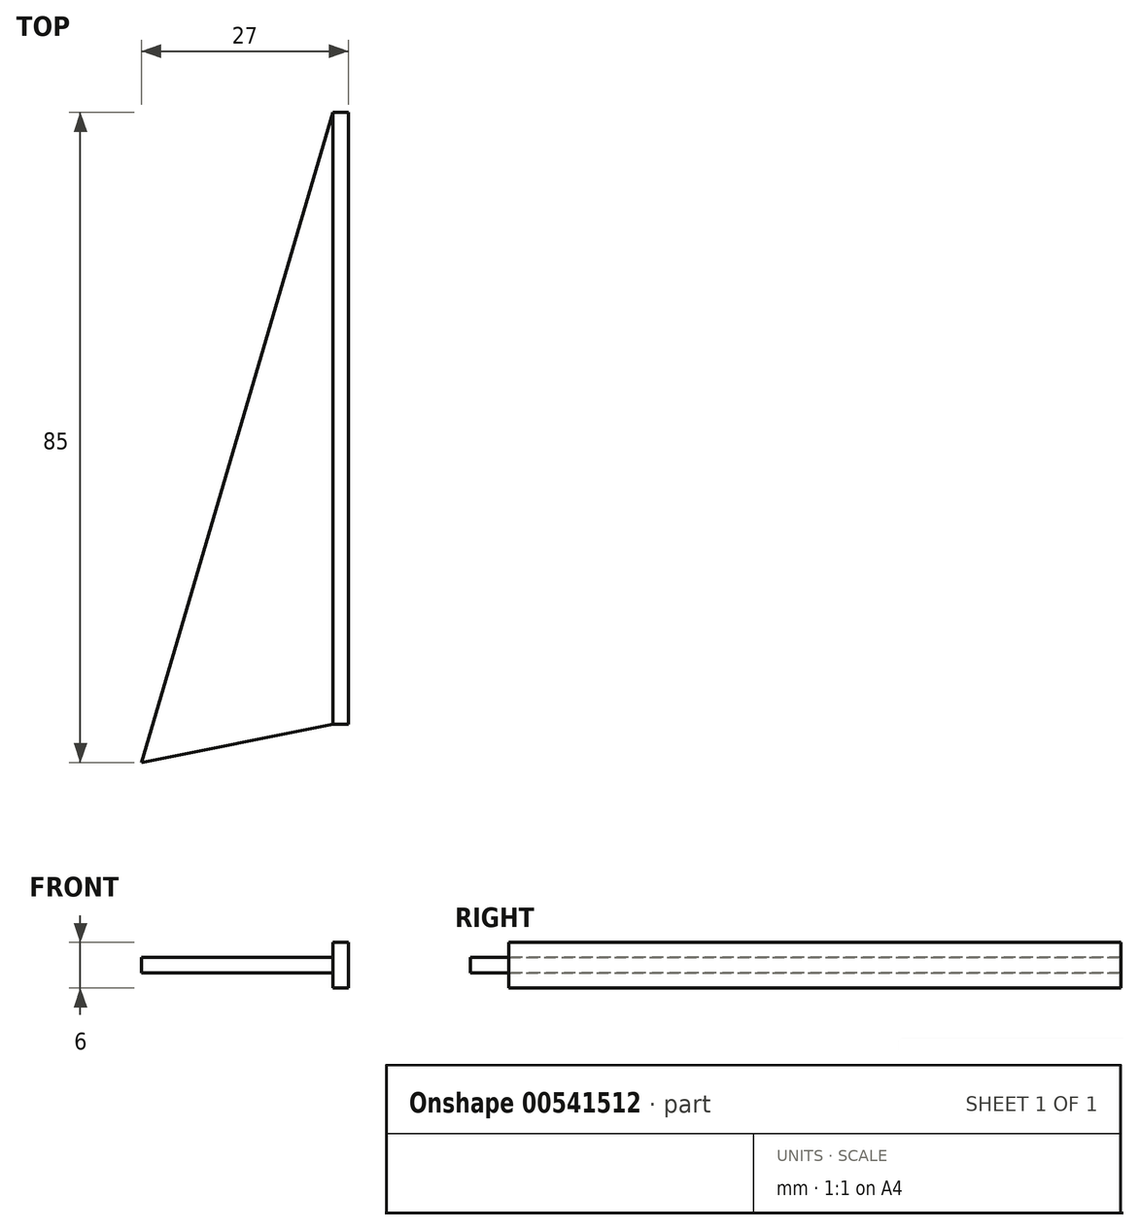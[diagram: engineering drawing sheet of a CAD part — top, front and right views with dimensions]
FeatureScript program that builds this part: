
annotation { "Feature Type Name" : "Feature", "Feature Type Description" : "" }
export const myFeature = defineFeature(function(context is Context, id is Id, definition is map)
    precondition{}
    {
        {
            var Q0;
            Q0=qCreatedBy(makeId("Top.planeOp"),FACE);
            var sketch = newSketch(context, id + "F0", { "sketchPlane" : qUnion([Q0])});
            skLineSegment(sketch, "E0", {"start": v(0, 0) * mm, "end": v(0, 80) * mm});
            skLineSegment(sketch, "E1", {"start": v(0, 80) * mm, "end": v(-25, -5) * mm});
            skLineSegment(sketch, "E2", {"start": v(-25, -5) * mm, "end": v(0, 0) * mm});
            skSolve(sketch);
        }
        {
            var Q0;
            Q0=makeQuery(id+"F0.imprint","IMPRINT",FACE,{"disambiguationData":[TD([[makeQuery(id+"F0.imprint","IMPRINT",EDGE,{"derivedFrom":sQuery(id+"F0.wireOp",EDGE,"E0")}),1.0]])]});
            extrude(context, id + "F1", {"entities" : qUnion([Q0]), "depth" : 2 * mm});
        }
        {
            var Q0;
            Q0=makeQuery(id+"F1.opExtrude","SWEPT_FACE",FACE,{"disambiguationData":[OSD([sQuery(id+"F0.wireOp",EDGE,"E0")])]});
            extrude(context, id + "F2", {"entities" : qUnion([Q0]), "operationType" : NewBodyOperationType.ADD, "depth" : 2 * mm});
        }
        {
            var Q0;
            {var subQ0=sQuery(id+"F0.wireOp",EDGE,"E0");Q0=makeQuery(id+"F2.boolean.opBoolean","MERGE",FACE,{"derivedFrom":[makeQuery(id+"F1.opExtrude","CAP_FACE",FACE,{"disambiguationData":[OSD([subQ0,sQuery(id+"F0.wireOp",EDGE,"E1"),sQuery(id+"F0.wireOp",EDGE,"E2")])],"isStart":false}),makeQuery(id+"F2.opExtrude","SWEPT_FACE",FACE,{"disambiguationData":[OSD([subQ0]),TDD([makeQuery(id+"F1.opExtrude","CAP_EDGE",EDGE,{"disambiguationData":[OSD([subQ0])],"isStart":false})])]})]});}
            var sketch = newSketch(context, id + "F3", { "sketchPlane" : qUnion([Q0])});
            skLineSegment(sketch, "E3.bottom", {"start": v(0, 0) * mm, "end": v(2, 0) * mm});
            skLineSegment(sketch, "E3.top", {"start": v(0, 80) * mm, "end": v(2, 80) * mm});
            skLineSegment(sketch, "E3.left", {"start": v(0, 0) * mm, "end": v(0, 80) * mm});
            skLineSegment(sketch, "E3.right", {"start": v(2, 0) * mm, "end": v(2, 80) * mm});
            skSolve(sketch);
        }
        {
            var Q0;
            Q0=qSketchRegion(id+"F3",true);
            extrude(context, id + "F4", {"entities" : qUnion([Q0]), "operationType" : NewBodyOperationType.ADD, "depth" : 2 * mm});
        }
        {
            var Q0;
            Q0=qSketchRegion(id+"F3",true);
            extrude(context, id + "F5", {"entities" : qUnion([Q0]), "operationType" : NewBodyOperationType.ADD, "oppositeDirection" : true, "depth" : 4 * mm});
        }
    });
